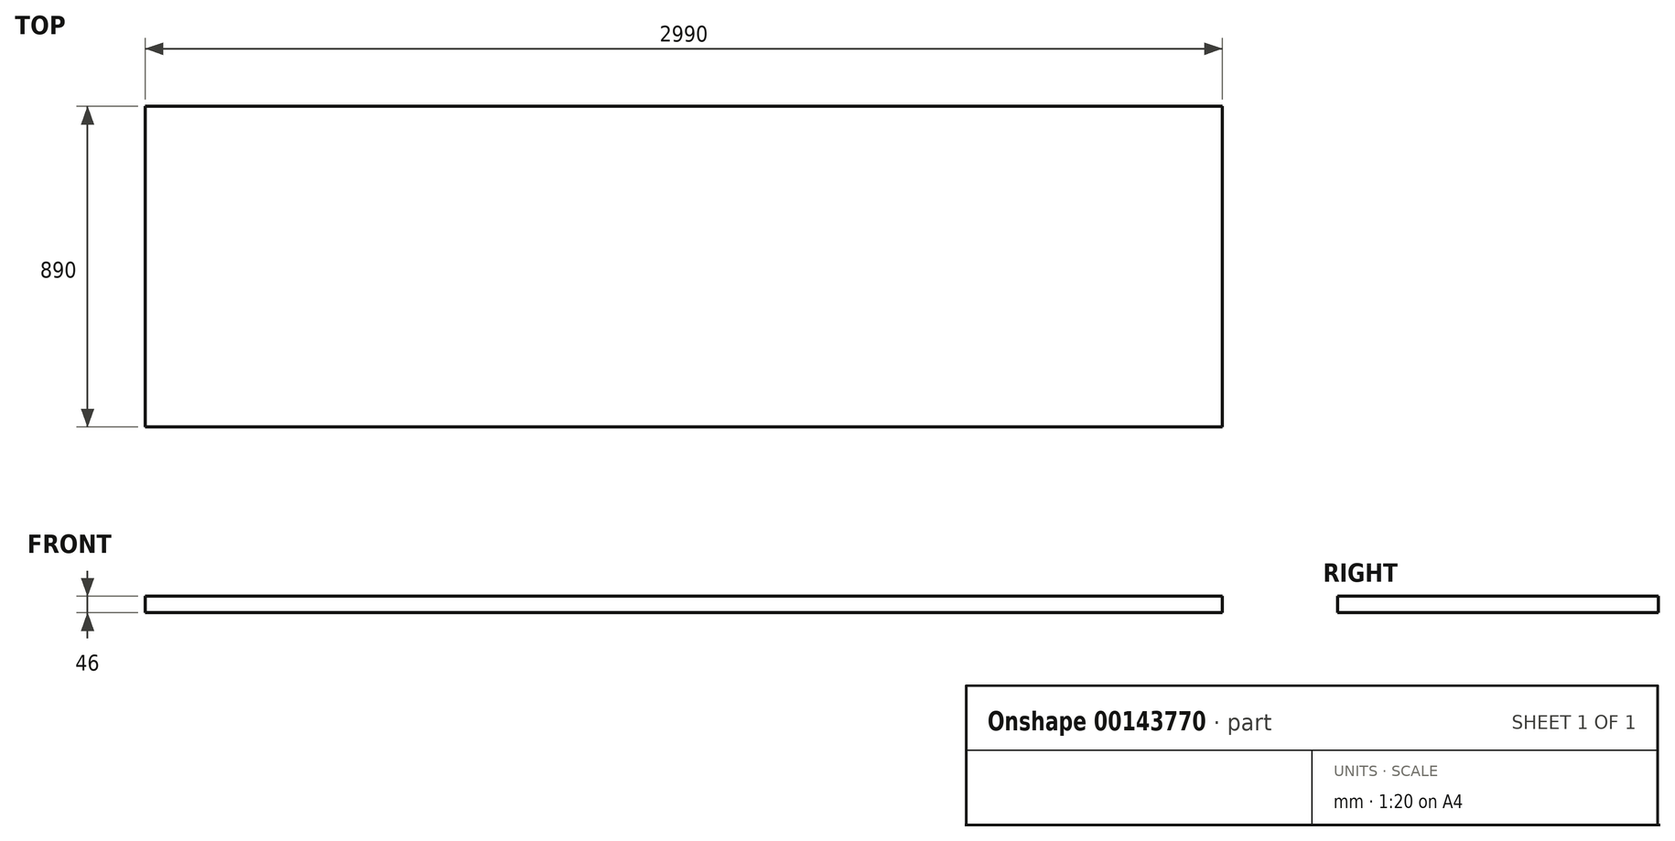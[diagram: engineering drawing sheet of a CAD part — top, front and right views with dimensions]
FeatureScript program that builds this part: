
annotation { "Feature Type Name" : "Feature", "Feature Type Description" : "" }
export const myFeature = defineFeature(function(context is Context, id is Id, definition is map)
    precondition{}
    {
        {
            var Q0;
            Q0=qCreatedBy(makeId("Top.planeOp"),FACE);
            var sketch = newSketch(context, id + "F0", { "sketchPlane" : qUnion([Q0])});
            skLineSegment(sketch, "E0.bottom", {"start": v(-1495, 445) * mm, "end": v(1495, 445) * mm});
            skLineSegment(sketch, "E0.top", {"start": v(-1495, -445) * mm, "end": v(1495, -445) * mm});
            skLineSegment(sketch, "E0.left", {"start": v(-1495, 445) * mm, "end": v(-1495, -445) * mm});
            skLineSegment(sketch, "E0.right", {"start": v(1495, 445) * mm, "end": v(1495, -445) * mm});
            skSolve(sketch);
        }
        {
            var Q0;
            Q0 = qSketchRegion(id + "F0", true);
            extrude(context, id + "F1", {"entities" : qUnion([Q0]), "endBound" : BoundingType.SYMMETRIC, "depth" : 46 * mm});
        }
    });
